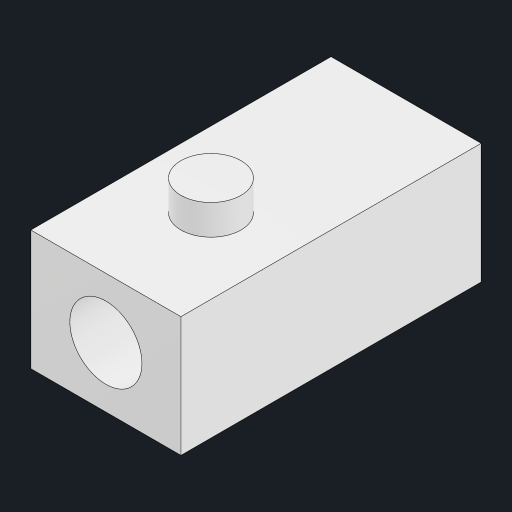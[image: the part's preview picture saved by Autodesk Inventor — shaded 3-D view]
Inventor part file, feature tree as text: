
AUTODESK INVENTOR PART (.ipt)
format: ipt  version: 2023 (Build 270158000, 158)  size: 118,784 bytes
history: native  units: mm
features: sketch x3, extrude x2, other x1, hole x1
ambient origin geometry x8: Origin, YZ Plane, XZ Plane, XY Plane, X Axis, Y Axis, Z Axis, Center Point
bodies: Body1 (feature_tree)
feature tree (7):
  other  "ソリッド1"
  extrude  "押し出し1"  Depth=5.0mm
  extrude  "押し出し2"  Depth=4.0mm TaperAngle=0.0deg
  hole  "穴4"  [1 undecoded]
  sketch  "スケッチ1"
  sketch  "スケッチ2"
  sketch  "スケッチ9"
note: 1 required parameter value undecoded (feature->parameter linkage not recoverable at this tier; creation-order binding heuristic only, values carry confidence <= 0.55)
